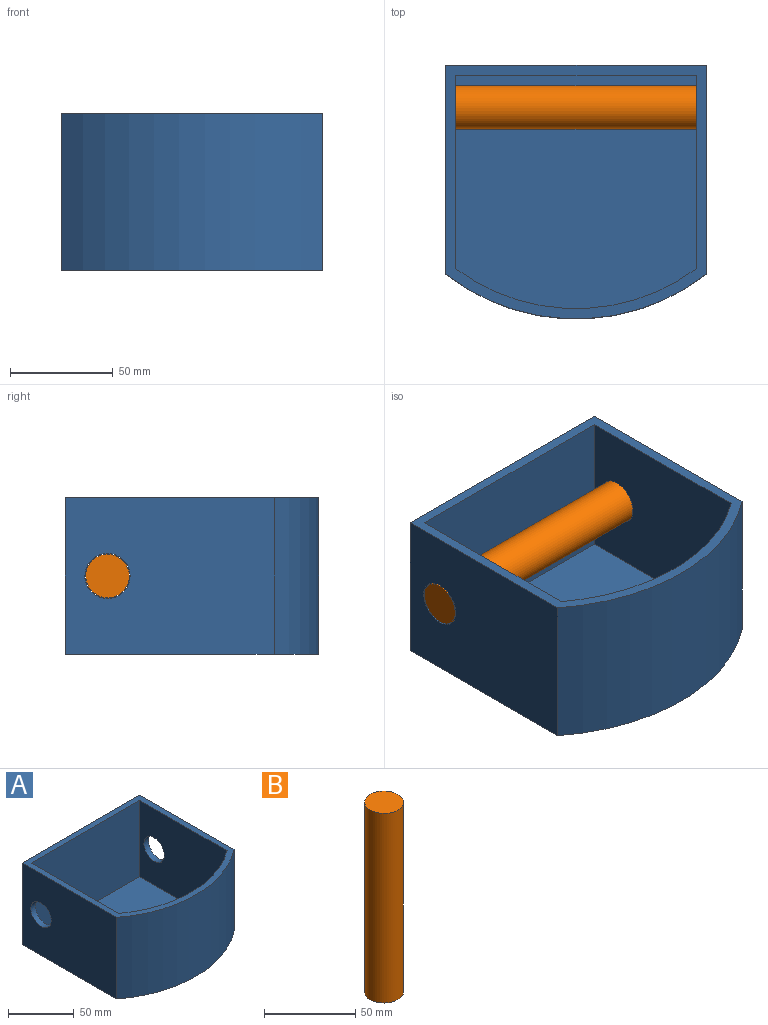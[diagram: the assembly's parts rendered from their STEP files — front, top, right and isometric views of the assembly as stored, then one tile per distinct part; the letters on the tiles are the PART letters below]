
ASSEMBLY  parts=2 mates=1
PART A: 13 faces, bbox 127x123.5x76.2 mm
  f0: plane 101.6x76.2mm, normal (-1,0,0), area 7361.8mm2, adj f1,f3,f4,f5,f12
  f1: cylinder r=103.07mm len=127mm, axis (0,0,-1), area 10426.3mm2, adj f0,f2,f4,f5
  f2: plane 101.6x76.2mm, normal (1,0,0), area 7361.8mm2, adj f1,f3,f4,f5,f11
  f3: plane 127x76.2mm, normal (0,1,0), area 9677.4mm2, adj f0,f2,f4,f5
  f4: plane 127x123.48mm, normal (0,0,1), area 2244.1mm2, adj f0,f1,f2,f3,f6,f7,f8,f9
  f5: plane 127x123.48mm, normal (0,0,-1), area 14799.4mm2, adj f0,f1,f2,f3
  f6: plane 94.13x71.2mm, normal (1,0,0), area 6321.6mm2, adj f4,f7,f9,f10,f12
  f7: cylinder r=98.07mm len=117mm, axis (0,0,-1), area 8925.8mm2, adj f4,f6,f8,f10
  f8: plane 94.13x71.2mm, normal (-1,0,0), area 6321.6mm2, adj f4,f7,f9,f10,f11
  f9: plane 117x71.2mm, normal (0,-1,0), area 8330.4mm2, adj f4,f6,f8,f10
  f10: plane 117x113.48mm, normal (0,0,1), area 12555.2mm2, adj f6,f7,f8,f9
  f11: cylinder r=11mm len=22mm, axis (1,0,0), area 345.6mm2, adj f2,f8
  f12: cylinder r=11mm len=22mm, axis (1,0,0), area 345.6mm2, adj f0,f6
PART B: 3 faces, bbox 21.3x21.3x127 mm
  f0: cylinder r=10.62mm len=127mm, axis (0,0,-1), area 8478.4mm2, adj f1,f2
  f1: plane 21.25x21.25mm, normal (0,0,1), area 354.7mm2, adj f0
  f2: plane 21.25x21.25mm, normal (0,0,-1), area 354.7mm2, adj f0
PLACE A at identity fixed
PLACE B rot(axis=(0.53,0.67,0.53),112.7deg) t=(-63.5,30.3,38.1)mm
MATE revolute B.f0 <-> A.f11  axis (1,0,0) through (63.5,30.3,38.1)mm
